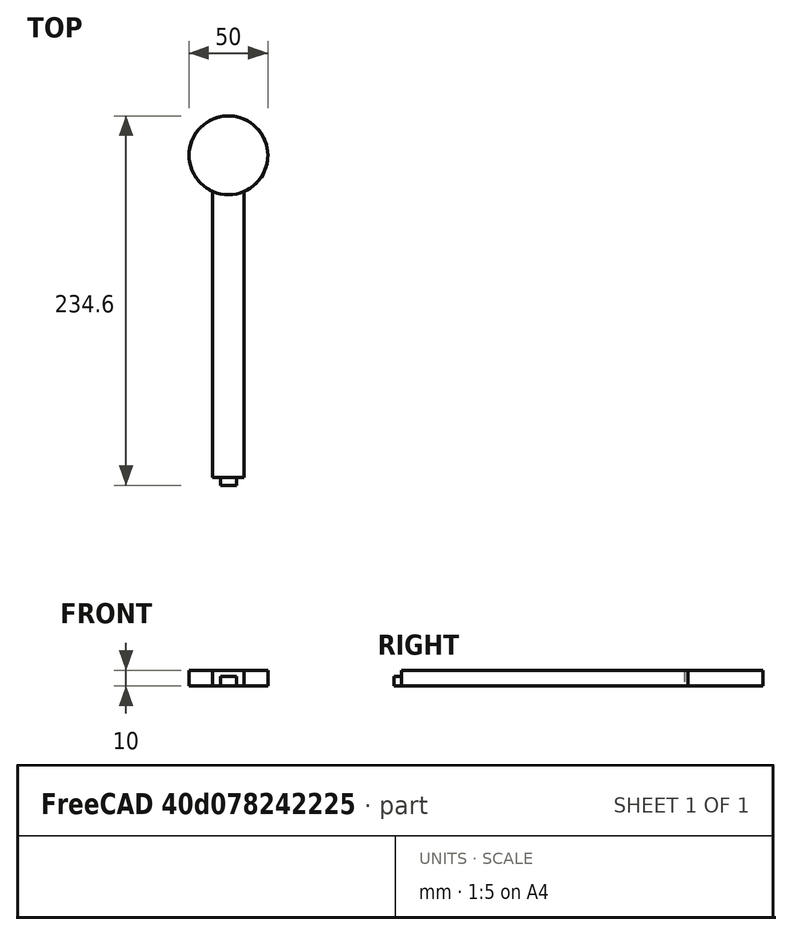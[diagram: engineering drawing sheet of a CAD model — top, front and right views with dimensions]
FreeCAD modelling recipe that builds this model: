
FCSTD DOCUMENT  (FreeCAD 0.16R)
Label: 26-50mmFauxRoue
License: All rights reserved
LicenseURL: http://en.wikipedia.org/wiki/All_rights_reserved
objects: Sketcher::SketchObject×3, PartDesign::Pad×3, Mesh::Feature×1
note: 9 computed .brp shape members not serialized (recipe doc carries the construction recipe); baked Part::Feature solids carry a one-line shape summary decoded from their .brp

FEATURE [Sketcher::SketchObject] Sketch
  sketch-geometry (2):
    g0: Circle CenterX=0 CenterY=204.6 CenterZ=0 NormalX=0 NormalY=0 NormalZ=1 Radius=25
    g1: LineSegment [constr] StartX=-99.2441 StartY=179.6 StartZ=0 EndX=99.2441 EndY=179.6 EndZ=0
  constraints (6):
    c: Radius(g0) = 25
    c: PointOnObject(g0,g-2)
    c: Horizontal(g1)
    c: Symmetric(g1,g1,g-2)
    c: Tangent(g0,g1)
    c: DistanceY(g1) = 179.6
FEATURE [PartDesign::Pad] Pad
  Length = 10
  Length2 = 100
  Sketch = -> Sketch
  Type = 0
FEATURE [Sketcher::SketchObject] Sketch001
  Placement = pos=(0,0,10) rot=(0,0,1;0rad)
  Support = -> Pad [Face3]
  sketch-geometry (4):
    g0: LineSegment StartX=-10 StartY=192.833 StartZ=0 EndX=10 EndY=192.833 EndZ=0
    g1: LineSegment StartX=10 StartY=192.833 StartZ=0 EndX=10 EndY=0 EndZ=0
    g2: LineSegment StartX=10 StartY=0 StartZ=0 EndX=-10 EndY=0 EndZ=0
    g3: LineSegment StartX=-10 StartY=0 StartZ=0 EndX=-10 EndY=192.833 EndZ=0
  constraints (12):
    c: Coincident(g0,g1)
    c: Coincident(g1,g2)
    c: Coincident(g2,g3)
    c: Coincident(g3,g0)
    c: Horizontal(g0)
    c: Horizontal(g2)
    c: Vertical(g1)
    c: Vertical(g3)
    c: PointOnObject(g1,g-1)
    c: Symmetric(g1,g2,g-2)
    c: DistanceY(g0) = 192.833
    c: Distance(g2) = 20
FEATURE [PartDesign::Pad] Pad001
  Length = 10
  Length2 = 100
  Reversed = true
  Sketch = -> Sketch001
  Type = 0
FEATURE [Sketcher::SketchObject] Sketch002
  ExternalGeometry = -> [Pad001]
  Placement = pos=(0,0,0) rot=(1,0,0;1.5708rad)
  Support = -> Pad001 [Face1]
  sketch-geometry (4):
    g0: LineSegment StartX=-5 StartY=6 StartZ=0 EndX=5 EndY=6 EndZ=0
    g1: LineSegment StartX=5 StartY=6 StartZ=0 EndX=5 EndY=0 EndZ=0
    g2: LineSegment StartX=5 StartY=0 StartZ=0 EndX=-5 EndY=0 EndZ=0
    g3: LineSegment StartX=-5 StartY=0 StartZ=0 EndX=-5 EndY=6 EndZ=0
  constraints (12):
    c: Coincident(g0,g1)
    c: Coincident(g1,g2)
    c: Coincident(g2,g3)
    c: Coincident(g3,g0)
    c: Horizontal(g0)
    c: Horizontal(g2)
    c: Vertical(g1)
    c: Vertical(g3)
    c: PointOnObject(g1,g-5)
    c: Symmetric(g1,g2,g-2)
    c: Distance(g0) = 10
    c: Distance(g1) = 6
FEATURE [PartDesign::Pad] Pad002
  Length = 5
  Length2 = 100
  Sketch = -> Sketch002
  Type = 0
FEATURE [Mesh::Feature] Mesh  label="Pad002 (Meshed)"
